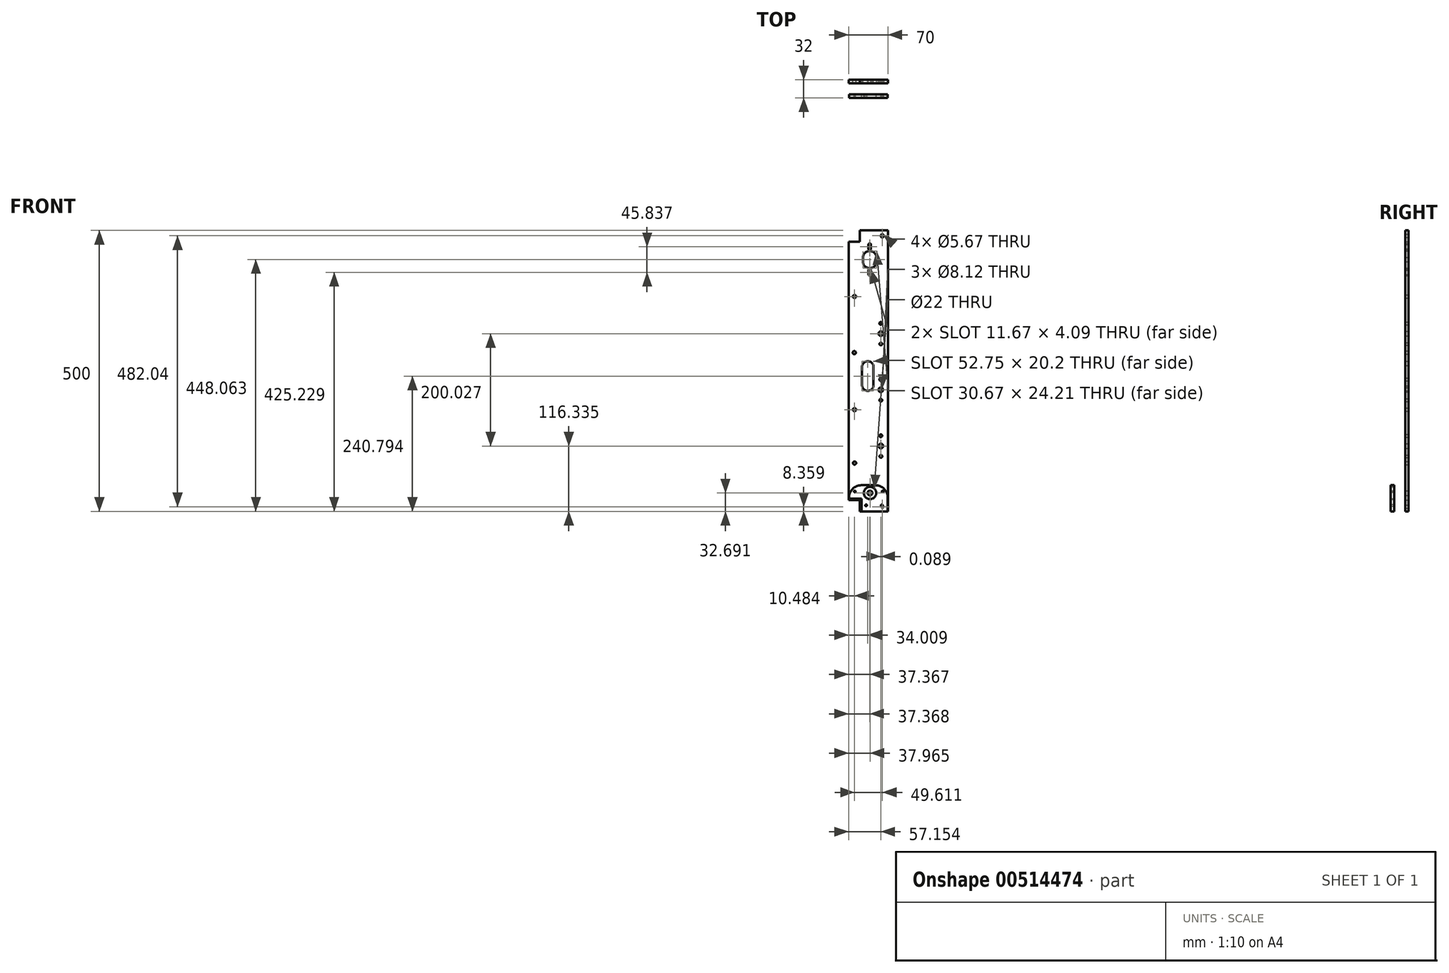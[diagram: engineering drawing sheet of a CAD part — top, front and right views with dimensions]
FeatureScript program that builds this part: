
annotation { "Feature Type Name" : "Feature", "Feature Type Description" : "" }
export const myFeature = defineFeature(function(context is Context, id is Id, definition is map)
    precondition{}
    {
        {
            var Q0;
            Q0=qCreatedBy(makeId("Front.planeOp"),FACE);
            var sketch = newSketch(context, id + "F0", { "sketchPlane" : qUnion([Q0])});
            skLineSegment(sketch, "E0", {"start": v(-15, 230) * mm, "end": v(-35, 230) * mm});
            skLineSegment(sketch, "E1", {"start": v(-35, 230) * mm, "end": v(-35, -230) * mm});
            skLineSegment(sketch, "E2", {"start": v(-35, -230) * mm, "end": v(-15, -230) * mm});
            skLineSegment(sketch, "E3", {"start": v(-15, -230) * mm, "end": v(-15, -250) * mm});
            skLineSegment(sketch, "E4", {"start": v(-15, -250) * mm, "end": v(35, -250) * mm});
            skLineSegment(sketch, "E5", {"start": v(35, -250) * mm, "end": v(35, 250) * mm});
            skLineSegment(sketch, "E6", {"start": v(35, 250) * mm, "end": v(-15, 250) * mm});
            skLineSegment(sketch, "E7", {"start": v(-15, 250) * mm, "end": v(-15, 230) * mm});
            skArc(sketch, "E8", {"start": v(14.47, 201.8) * mm, "mid": v(2.37, 213.4) * mm, "end": v(-9.74, 201.8) * mm});
            skArc(sketch, "E9", {"start": v(4.41, 225.1) * mm, "mid": v(2.37, 226.9) * mm, "end": v(0.32, 225.1) * mm});
            skArc(sketch, "E10", {"start": v(0.32, 217.04) * mm, "mid": v(2.37, 215.23) * mm, "end": v(4.41, 217.04) * mm});
            skLineSegment(sketch, "E11", {"start": v(0.32, 225.1) * mm, "end": v(0.32, 217.04) * mm});
            skLineSegment(sketch, "E12", {"start": v(4.41, 225.1) * mm, "end": v(4.41, 217.04) * mm});
            skArc(sketch, "E13", {"start": v(-9.74, 194.33) * mm, "mid": v(2.37, 182.73) * mm, "end": v(14.47, 194.33) * mm});
            skLineSegment(sketch, "E14", {"start": v(-9.74, 201.8) * mm, "end": v(-9.74, 194.33) * mm});
            skLineSegment(sketch, "E15", {"start": v(14.47, 201.8) * mm, "end": v(14.47, 194.33) * mm});
            skArc(sketch, "E16", {"start": v(4.41, 179.26) * mm, "mid": v(2.37, 181.06) * mm, "end": v(0.32, 179.26) * mm});
            skArc(sketch, "E17", {"start": v(0.32, 171.2) * mm, "mid": v(2.37, 169.4) * mm, "end": v(4.41, 171.2) * mm});
            skLineSegment(sketch, "E18", {"start": v(0.32, 179.26) * mm, "end": v(0.32, 171.2) * mm});
            skLineSegment(sketch, "E19", {"start": v(4.41, 179.26) * mm, "end": v(4.41, 171.2) * mm});
            skArc(sketch, "E20", {"start": v(9.11, 8.67) * mm, "mid": v(-1, 17.17) * mm, "end": v(-11.1, 8.67) * mm});
            skArc(sketch, "E21", {"start": v(-11.1, -26.63) * mm, "mid": v(-1, -35.58) * mm, "end": v(9.11, -26.63) * mm});
            skLineSegment(sketch, "E22", {"start": v(-11.1, 8.67) * mm, "end": v(-11.1, -26.63) * mm});
            skLineSegment(sketch, "E23", {"start": v(9.11, -26.63) * mm, "end": v(9.11, 8.67) * mm});
            skCircle(sketch, "E24", {"center": v(22.15, 66.36) * mm, "radius": 4.06 * mm});
            skCircle(sketch, "E25", {"center": v(22.06, 84.6) * mm, "radius": 2.42 * mm});
            skCircle(sketch, "E26", {"center": v(22.25, 47.9) * mm, "radius": 2.43 * mm});
            skCircle(sketch, "E27", {"center": v(22.06, -15.42) * mm, "radius": 2.42 * mm});
            skCircle(sketch, "E28", {"center": v(22.15, -33.65) * mm, "radius": 4.06 * mm});
            skCircle(sketch, "E29", {"center": v(22.25, -52.1) * mm, "radius": 2.43 * mm});
            skCircle(sketch, "E30", {"center": v(22.15, -115.43) * mm, "radius": 2.42 * mm});
            skCircle(sketch, "E31", {"center": v(22.24, -133.67) * mm, "radius": 4.06 * mm});
            skCircle(sketch, "E32", {"center": v(22.33, -152.12) * mm, "radius": 2.43 * mm});
            skCircle(sketch, "E33", {"center": v(2.93, -217.3) * mm, "radius": 4.25 * mm});
            skCircle(sketch, "E34", {"center": v(25.1, -241.64) * mm, "radius": 2.83 * mm});
            skCircle(sketch, "E35", {"center": v(-24.52, -163.97) * mm, "radius": 2.83 * mm});
            skCircle(sketch, "E36", {"center": v(-24.52, -68.96) * mm, "radius": 2.83 * mm});
            skCircle(sketch, "E37", {"center": v(-24.95, 32.48) * mm, "radius": 2.84 * mm});
            skCircle(sketch, "E38", {"center": v(-24.52, 132.39) * mm, "radius": 2.83 * mm});
            skCircle(sketch, "E39", {"center": v(24.75, 240.4) * mm, "radius": 2.83 * mm});
            skLineSegment(sketch, "E40", {"start": v(35, -230) * mm, "end": v(18.67, -230) * mm, "construction": true});
            skLineSegment(sketch, "E41", {"start": v(18.67, -230) * mm, "end": v(18.67, -210) * mm, "construction": true});
            skLineSegment(sketch, "E42", {"start": v(18.67, -210) * mm, "end": v(35, -210) * mm, "construction": true});
            skCircle(sketch, "E43", {"center": v(2.93, -217.3) * mm, "radius": 11 * mm, "construction": true});
            skLineSegment(sketch, "E44", {"start": v(-15, -230) * mm, "end": v(18.67, -230) * mm, "construction": true});
            skLineSegment(sketch, "E45", {"start": v(-15, -230) * mm, "end": v(-15, 230) * mm, "construction": true});
            skLineSegment(sketch, "E46", {"start": v(18.67, -230) * mm, "end": v(18.67, -250) * mm, "construction": true});
            skPoint(sketch, "E46.endSnap0", {"position": v(10, -250) * mm});
            skLineSegment(sketch, "E47", {"start": v(18.67, -210) * mm, "end": v(18.67, 250) * mm, "construction": true});
            skSolve(sketch);
        }
        {
            var Q0;
            Q0=makeQuery(id+"F0.imprint","IMPRINT",FACE,{"disambiguationData":[TD([[makeQuery(id+"F0.imprint","IMPRINT",EDGE,{"derivedFrom":sQuery(id+"F0.wireOp",EDGE,"E0")}),1.0]])]});
            extrude(context, id + "F1", {"entities" : qUnion([Q0]), "depth" : 6 * mm});
        }
        {
            var Q0;
            Q0=makeQuery(id+"F1.opExtrude","CAP_FACE",FACE,{"disambiguationData":[OSD([sQuery(id+"F0.wireOp",EDGE,"E0"),sQuery(id+"F0.wireOp",EDGE,"E1"),sQuery(id+"F0.wireOp",EDGE,"E2"),sQuery(id+"F0.wireOp",EDGE,"E3"),sQuery(id+"F0.wireOp",EDGE,"E4"),sQuery(id+"F0.wireOp",EDGE,"E5"),sQuery(id+"F0.wireOp",EDGE,"E6"),sQuery(id+"F0.wireOp",EDGE,"E7"),sQuery(id+"F0.wireOp",EDGE,"E8"),sQuery(id+"F0.wireOp",EDGE,"E9"),sQuery(id+"F0.wireOp",EDGE,"E10"),sQuery(id+"F0.wireOp",EDGE,"E11"),sQuery(id+"F0.wireOp",EDGE,"E12"),sQuery(id+"F0.wireOp",EDGE,"E13"),sQuery(id+"F0.wireOp",EDGE,"E14"),sQuery(id+"F0.wireOp",EDGE,"E15"),sQuery(id+"F0.wireOp",EDGE,"E16"),sQuery(id+"F0.wireOp",EDGE,"E17"),sQuery(id+"F0.wireOp",EDGE,"E18"),sQuery(id+"F0.wireOp",EDGE,"E19"),sQuery(id+"F0.wireOp",EDGE,"E20"),sQuery(id+"F0.wireOp",EDGE,"E21"),sQuery(id+"F0.wireOp",EDGE,"E22"),sQuery(id+"F0.wireOp",EDGE,"E23"),sQuery(id+"F0.wireOp",EDGE,"E24"),sQuery(id+"F0.wireOp",EDGE,"E25"),sQuery(id+"F0.wireOp",EDGE,"E26"),sQuery(id+"F0.wireOp",EDGE,"E27"),sQuery(id+"F0.wireOp",EDGE,"E28"),sQuery(id+"F0.wireOp",EDGE,"E29"),sQuery(id+"F0.wireOp",EDGE,"E30"),sQuery(id+"F0.wireOp",EDGE,"E31"),sQuery(id+"F0.wireOp",EDGE,"E32"),sQuery(id+"F0.wireOp",EDGE,"E33"),sQuery(id+"F0.wireOp",EDGE,"E34"),sQuery(id+"F0.wireOp",EDGE,"E35"),sQuery(id+"F0.wireOp",EDGE,"E36"),sQuery(id+"F0.wireOp",EDGE,"E37"),sQuery(id+"F0.wireOp",EDGE,"E38"),sQuery(id+"F0.wireOp",EDGE,"E39")])],"isStart":false});
            cPlane(context, id + "F2", {"entities" : qUnion([Q0]), "cplaneType" : CPlaneType.OFFSET, "offset" : 20 * mm, "width" : 150 * mm, "height" : 150 * mm});
        }
        {
            var Q0;
            Q0=qCreatedBy(id+"F2.planeOp",FACE);
            var sketch = newSketch(context, id + "F3", { "sketchPlane" : qUnion([Q0])});
            skLineSegment(sketch, "E48", {"start": v(-34.43, -227.19) * mm, "end": v(-12.05, -227.19) * mm});
            skLineSegment(sketch, "E49", {"start": v(-12.05, -227.19) * mm, "end": v(-12.05, -249.98) * mm});
            skLineSegment(sketch, "E50", {"start": v(-12.05, -249.98) * mm, "end": v(34.58, -249.98) * mm});
            skLineSegment(sketch, "E51", {"start": v(34.58, -249.98) * mm, "end": v(34.58, -225.48) * mm});
            skLineSegment(sketch, "E52", {"start": v(12.58, -203.48) * mm, "end": v(-12.43, -203.48) * mm});
            skLineSegment(sketch, "E53", {"start": v(-34.43, -225.48) * mm, "end": v(-34.43, -227.19) * mm});
            skCircle(sketch, "E54", {"center": v(-24.06, -214.56) * mm, "radius": 1.52 * mm});
            skCircle(sketch, "E55", {"center": v(-4, -239.22) * mm, "radius": 1.52 * mm});
            skCircle(sketch, "E56", {"center": v(25.55, -214.56) * mm, "radius": 1.52 * mm});
            skCircle(sketch, "E57", {"center": v(23.94, -239.22) * mm, "radius": 1.52 * mm});
            skCircle(sketch, "E58", {"center": v(2.97, -217.3) * mm, "radius": 11 * mm});
            skPoint(sketch, "E59.visualSharp", {"position": v(-34.43, -203.48) * mm});
            skArc(sketch, "E59.filletArc", {"start": v(-12.43, -203.48) * mm, "mid": v(-27.99, -209.93) * mm, "end": v(-34.43, -225.48) * mm});
            skPoint(sketch, "E60.visualSharp", {"position": v(34.58, -203.48) * mm});
            skArc(sketch, "E60.filletArc", {"start": v(34.58, -225.48) * mm, "mid": v(28.14, -209.93) * mm, "end": v(12.58, -203.48) * mm});
            skLineSegment(sketch, "E61.bottom", {"start": v(-14.06, -231.3) * mm, "end": v(-34.06, -231.3) * mm, "construction": true});
            skLineSegment(sketch, "E61.top", {"start": v(-14.06, -197.82) * mm, "end": v(-34.06, -197.82) * mm, "construction": true});
            skLineSegment(sketch, "E61.left", {"start": v(-14.06, -231.3) * mm, "end": v(-14.06, -197.82) * mm, "construction": true});
            skLineSegment(sketch, "E61.right", {"start": v(-34.06, -231.3) * mm, "end": v(-34.06, -197.82) * mm, "construction": true});
            skLineSegment(sketch, "E62.bottom", {"start": v(15.55, -233.56) * mm, "end": v(35.55, -233.56) * mm, "construction": true});
            skLineSegment(sketch, "E62.top", {"start": v(15.55, -195.56) * mm, "end": v(35.55, -195.56) * mm, "construction": true});
            skLineSegment(sketch, "E62.left", {"start": v(15.55, -233.56) * mm, "end": v(15.55, -195.56) * mm, "construction": true});
            skLineSegment(sketch, "E62.right", {"start": v(35.55, -233.56) * mm, "end": v(35.55, -195.56) * mm, "construction": true});
            skSolve(sketch);
        }
        {
            var Q0;
            Q0=makeQuery(id+"F3.imprint","IMPRINT",FACE,{"disambiguationData":[TD([[makeQuery(id+"F3.imprint","IMPRINT",EDGE,{"derivedFrom":sQuery(id+"F3.wireOp",EDGE,"E48")}),1.0]])]});
            extrude(context, id + "F4", {"entities" : qUnion([Q0]), "depth" : 6 * mm});
        }
    });
